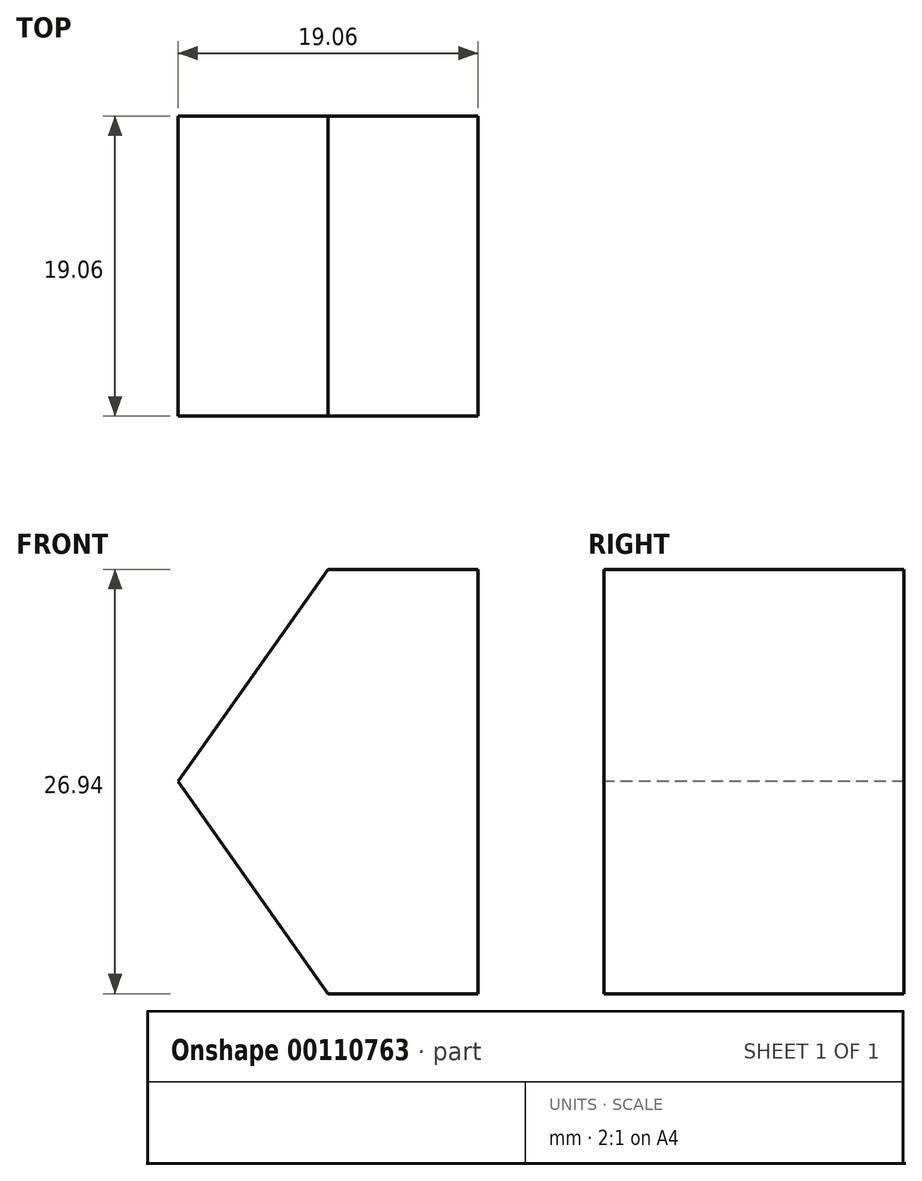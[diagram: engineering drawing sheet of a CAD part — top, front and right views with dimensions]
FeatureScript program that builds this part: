
annotation { "Feature Type Name" : "Feature", "Feature Type Description" : "" }
export const myFeature = defineFeature(function(context is Context, id is Id, definition is map)
    precondition{}
    {
        {
            var Q0;
            Q0=qCreatedBy(makeId("Front.planeOp"),FACE);
            var sketch = newSketch(context, id + "F0", { "sketchPlane" : qUnion([Q0])});
            skLineSegment(sketch, "E0", {"start": v(0, -27.28) * mm, "end": v(0, 25.6) * mm, "construction": true});
            skLineSegment(sketch, "E1.bottom", {"start": v(9.52, -13.47) * mm, "end": v(-9.53, -13.47) * mm});
            skLineSegment(sketch, "E1.top", {"start": v(9.53, 13.47) * mm, "end": v(-9.52, 13.47) * mm});
            skLineSegment(sketch, "E1.left", {"start": v(9.53, -13.47) * mm, "end": v(9.53, 13.47) * mm});
            skLineSegment(sketch, "E1.right", {"start": v(-9.53, -13.47) * mm, "end": v(-9.53, 13.47) * mm});
            skPoint(sketch, "E1.middle", {"position": v(0, 0) * mm});
            skSolve(sketch);
        }
        {
            var Q0;
            Q0=qSketchRegion(id+"F0",true);
            extrude(context, id + "F1", {"entities" : qUnion([Q0]), "depth" : 9.52 * mm, "hasSecondDirection" : true, "secondDirectionOppositeDirection" : true, "secondDirectionDepth" : 9.52 * mm});
        }
        {
            var Q0;
            Q0=qCreatedBy(makeId("Front.planeOp"),FACE);
            var sketch = newSketch(context, id + "F2", { "sketchPlane" : qUnion([Q0])});
            skLineSegment(sketch, "E2", {"start": v(-9.53, 0) * mm, "end": v(0, 13.47) * mm});
            skLineSegment(sketch, "E3", {"start": v(-9.53, 0) * mm, "end": v(0, -13.47) * mm});
            skLineSegment(sketch, "E4.0", {"start": v(0, 13.47) * mm, "end": v(-9.53, 13.47) * mm});
            skLineSegment(sketch, "E4.1", {"start": v(-9.53, -13.47) * mm, "end": v(-9.53, 13.47) * mm});
            skLineSegment(sketch, "E4.2", {"start": v(0, -13.47) * mm, "end": v(-9.53, -13.47) * mm});
            skPoint(sketch, "E5.orphan", {"position": v(9.53, 13.47) * mm});
            skPoint(sketch, "E6.orphan", {"position": v(9.52, -13.47) * mm});
            skSolve(sketch);
        }
        {
            var Q0;
            Q0=qSketchRegion(id+"F2",true);
            extrude(context, id + "F3", {"entities" : qUnion([Q0]), "operationType" : NewBodyOperationType.REMOVE, "endBound" : BoundingType.THROUGH_ALL, "oppositeDirection" : true, "depth" : 25.4 * mm, "hasSecondDirection" : true, "secondDirectionBound" : SecondDirectionBoundingType.THROUGH_ALL, "secondDirectionOppositeDirection" : false, "secondDirectionDepth" : 25.4 * mm});
        }
    });
